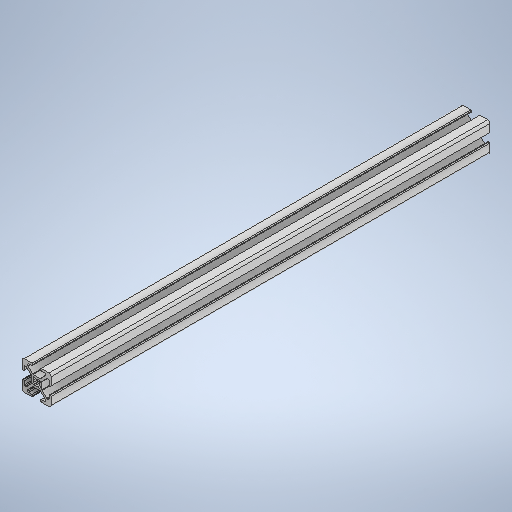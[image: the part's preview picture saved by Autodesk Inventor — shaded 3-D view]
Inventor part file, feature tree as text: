
AUTODESK INVENTOR PART (.ipt)
format: ipt  version: 2025 (Build 290162000, 162)  size: 476,672 bytes
history: native  units: mm
features: sketch x2, extrude x1, hole x1, mirror x1
ambient origin geometry x8: Origin, YZ Plane, XZ Plane, XY Plane, X Axis, Y Axis, Z Axis, Center Point
bodies: Solid1 (feature_tree)
feature tree (5):
  extrude  "Extrusion1"  Depth=2.384mm
  hole  "Hole1"  [1 undecoded]
  mirror  "Mirror1"
  sketch  "Sketch1"  dims[d0=300.699mm d1=0.0mm]
  sketch  "Sketch2"  dims[d2=5.0mm d3=6.0mm d4=4.0mm d5=2.0mm d6=90.0deg d7=8.0mm d8=20.594885mm d9=2.384mm d10=8.0mm d11=0.0625mm d12=0.75mm d13=0.375mm]
note: 1 required parameter value undecoded (feature->parameter linkage not recoverable at this tier; creation-order binding heuristic only, values carry confidence <= 0.55)
